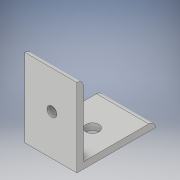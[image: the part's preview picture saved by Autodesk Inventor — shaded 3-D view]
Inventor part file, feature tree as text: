
AUTODESK INVENTOR PART (.ipt)
format: ipt  version: 2017 (Build 210142000, 142)  size: 118,272 bytes
history: native  units: in
note: dims shown in document units (in); Inventor stores cm internally (conversion verified against a paired STEP export)
features: extrude x2, fillet x2, hole x2, sketch x2
ambient origin geometry x8: Origin, YZ Plane, XZ Plane, XY Plane, X Axis, Y Axis, Z Axis, Center Point
bodies: Solid1 (feature_tree)
feature tree (8):
  extrude  "Extrusion1"  Depth=1.5in
  fillet  "Fillet1"  Radius=0.125in
  extrude  "Extrusion2"  Depth=0.125in
  fillet  "Fillet2"  Radius=1.375in
  hole  "Hole1"  [1 undecoded]
  hole  "Hole2"  [1 undecoded]
  sketch  "Sketch1"  dims[d0=1.0in d1=1.5in d2=0.125in d3=0.0in]
  sketch  "Sketch2"  dims[d4=0.125in d5=0.125in d6=1.375in d7=0.0in d8=0.125in d18=1.0in d19=1.0in d11=0.25in d12=0.75in d13=0.375in d14=0.25in d15=0.5635in d16=1.0in d17=0.8108in d20=1.0in d21=1.0in d22=0.1875in d23=0.75in d24=0.375in d25=0.25in d26=0.5635in d27=1.0in d28=0.8108in]
note: 2 required parameter values undecoded (feature->parameter linkage not recoverable at this tier; creation-order binding heuristic only, values carry confidence <= 0.55)
